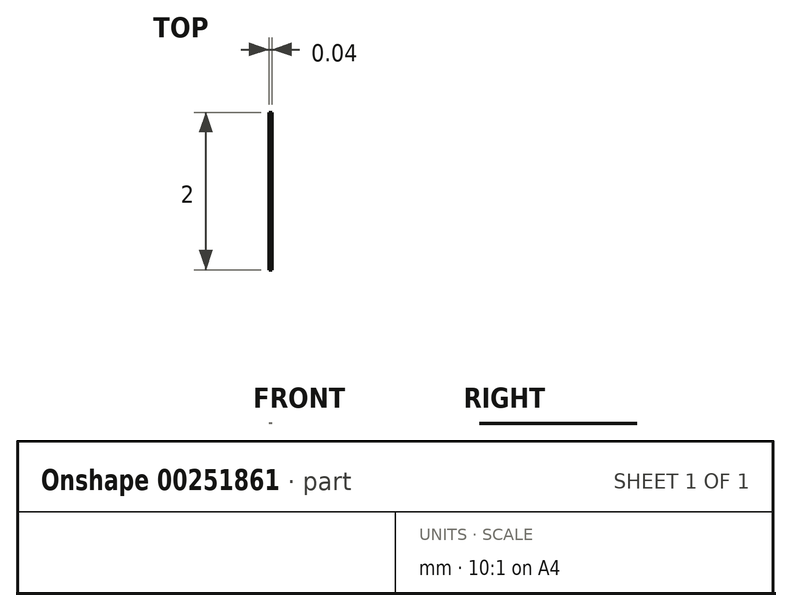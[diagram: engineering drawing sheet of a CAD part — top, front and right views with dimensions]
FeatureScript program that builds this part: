
annotation { "Feature Type Name" : "Feature", "Feature Type Description" : "" }
export const myFeature = defineFeature(function(context is Context, id is Id, definition is map)
    precondition{}
    {
        {
            var Q0;
            Q0=qCreatedBy(makeId("Front.planeOp"),FACE);
            var sketch = newSketch(context, id + "F0", { "sketchPlane" : qUnion([Q0])});
            skLineSegment(sketch, "E0.bottom", {"start": v(15, 1.5) * mm, "end": v(-15, 1.5) * mm});
            skLineSegment(sketch, "E0.top", {"start": v(15, -1.5) * mm, "end": v(-15, -1.5) * mm});
            skPoint(sketch, "E0.middle", {"position": v(0, 0) * mm});
            skLineSegment(sketch, "E1.bottom", {"start": v(29.98, 3) * mm, "end": v(20.25, 3) * mm});
            skLineSegment(sketch, "E1.top", {"start": v(29.98, -3) * mm, "end": v(20.25, -3) * mm});
            skLineSegment(sketch, "E1.right", {"start": v(14.98, -1.5) * mm, "end": v(14.98, -1.51) * mm});
            skPoint(sketch, "E1.middle", {"position": v(22.48, 0) * mm});
            skLineSegment(sketch, "E2.bottom", {"start": v(34.99, 7.5) * mm, "end": v(29.99, 7.5) * mm});
            skLineSegment(sketch, "E2.top", {"start": v(34.99, -7.5) * mm, "end": v(29.99, -7.5) * mm});
            skLineSegment(sketch, "E2.left", {"start": v(34.99, 7.5) * mm, "end": v(34.99, -7.5) * mm});
            skPoint(sketch, "E2.middle", {"position": v(32.49, 0) * mm});
            skLineSegment(sketch, "E3.bottom", {"start": v(-30.02, 7.5) * mm, "end": v(-35.02, 7.5) * mm});
            skLineSegment(sketch, "E3.top", {"start": v(-30.02, -7.5) * mm, "end": v(-35.02, -7.5) * mm});
            skLineSegment(sketch, "E3.right", {"start": v(-35.02, 7.5) * mm, "end": v(-35.02, -7.5) * mm});
            skPoint(sketch, "E3.middle", {"position": v(-32.52, 0) * mm});
            skArc(sketch, "E4", {"start": v(14.96, 1.5) * mm, "mid": v(14.98, 1.5) * mm, "end": v(15, 1.5) * mm});
            skLineSegment(sketch, "E5.bottom", {"start": v(-20.27, -3) * mm, "end": v(-30.02, -3) * mm});
            skLineSegment(sketch, "E5.top", {"start": v(-20.27, 3) * mm, "end": v(-30.02, 3) * mm});
            skPoint(sketch, "E5.middle", {"position": v(-22.52, 0) * mm});
            skArc(sketch, "E6", {"start": v(-15.04, 1.5) * mm, "mid": v(-15.02, 1.5) * mm, "end": v(-15, 1.5) * mm});
            skArc(sketch, "E7", {"start": v(-15, -1.5) * mm, "mid": v(-15.02, -1.5) * mm, "end": v(-15.04, -1.5) * mm});
            skArc(sketch, "E8", {"start": v(15, -1.51) * mm, "mid": v(15, -1.51) * mm, "end": v(14.98, -1.51) * mm});
            skArc(sketch, "E9", {"start": v(-20.27, 3) * mm, "mid": v(-17.74, 1.88) * mm, "end": v(-15, 1.5) * mm});
            skArc(sketch, "E10", {"start": v(-15, -1.5) * mm, "mid": v(-17.74, -1.88) * mm, "end": v(-20.27, -3) * mm});
            skArc(sketch, "E11", {"start": v(14.96, 1.5) * mm, "mid": v(17.71, 1.88) * mm, "end": v(20.25, 3) * mm});
            skLineSegment(sketch, "E12", {"start": v(15, -1.5) * mm, "end": v(15, -1.51) * mm});
            skArc(sketch, "E13", {"start": v(20.25, -3) * mm, "mid": v(17.71, -1.88) * mm, "end": v(14.96, -1.5) * mm});
            skLineSegment(sketch, "E14", {"start": v(-30.02, 7.5) * mm, "end": v(-30.02, 3) * mm});
            skLineSegment(sketch, "E15", {"start": v(-30.02, -3) * mm, "end": v(-30.02, -7.5) * mm});
            skLineSegment(sketch, "E16", {"start": v(29.99, 7.5) * mm, "end": v(29.98, 3) * mm});
            skLineSegment(sketch, "E17", {"start": v(29.98, -3) * mm, "end": v(29.99, -7.5) * mm});
            skSolve(sketch);
        }
        {
            var Q0;
            Q0=makeQuery(id+"F0.imprint","IMPRINT",FACE,{"disambiguationData":[TD([[makeQuery(id+"F0.imprint","IMPRINT",EDGE,{"derivedFrom":sQuery(id+"F0.wireOp",EDGE,"E0.bottom")}),1.0]])]});
            extrude(context, id + "F1", {"entities" : qUnion([Q0]), "depth" : 2 * mm});
        }
    });
